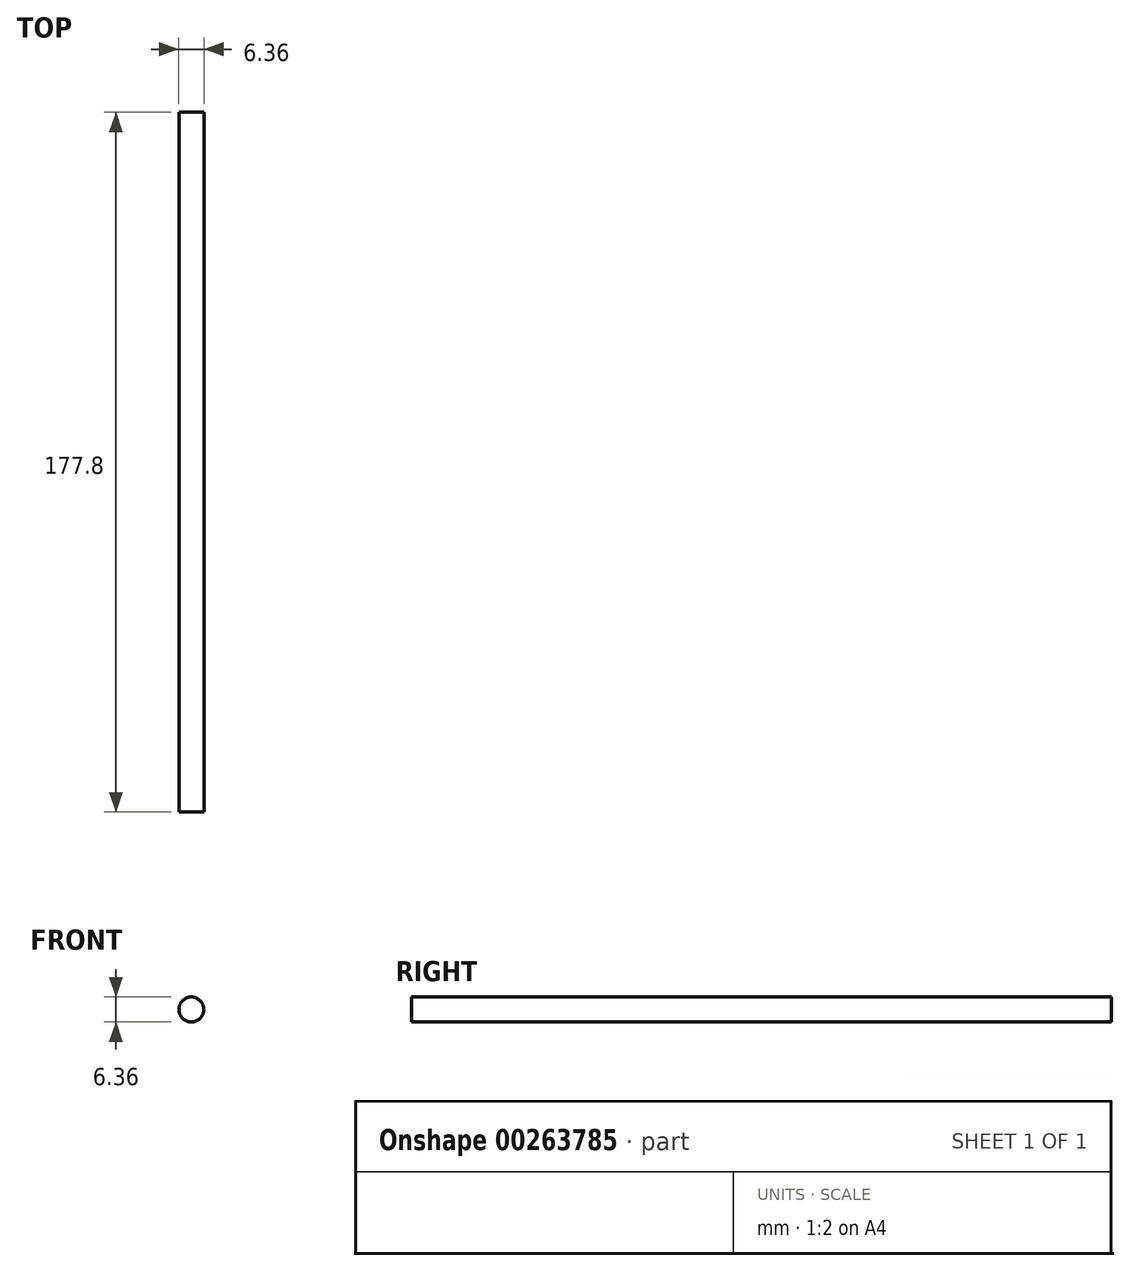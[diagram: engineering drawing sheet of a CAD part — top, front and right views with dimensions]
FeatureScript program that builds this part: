
annotation { "Feature Type Name" : "Feature", "Feature Type Description" : "" }
export const myFeature = defineFeature(function(context is Context, id is Id, definition is map)
    precondition{}
    {
        {
            var Q0;
            Q0=qCreatedBy(makeId("Front.planeOp"),FACE);
            var sketch = newSketch(context, id + "F0", { "sketchPlane" : qUnion([Q0])});
            skCircle(sketch, "E0", {"center": v(0, 0) * mm, "radius": 3.18 * mm});
            skSolve(sketch);
        }
        {
            var Q0;
            Q0=qSketchRegion(id+"F0",true);
            extrude(context, id + "F1", {"entities" : qUnion([Q0]), "depth" : 177.8 * mm});
        }
    });
